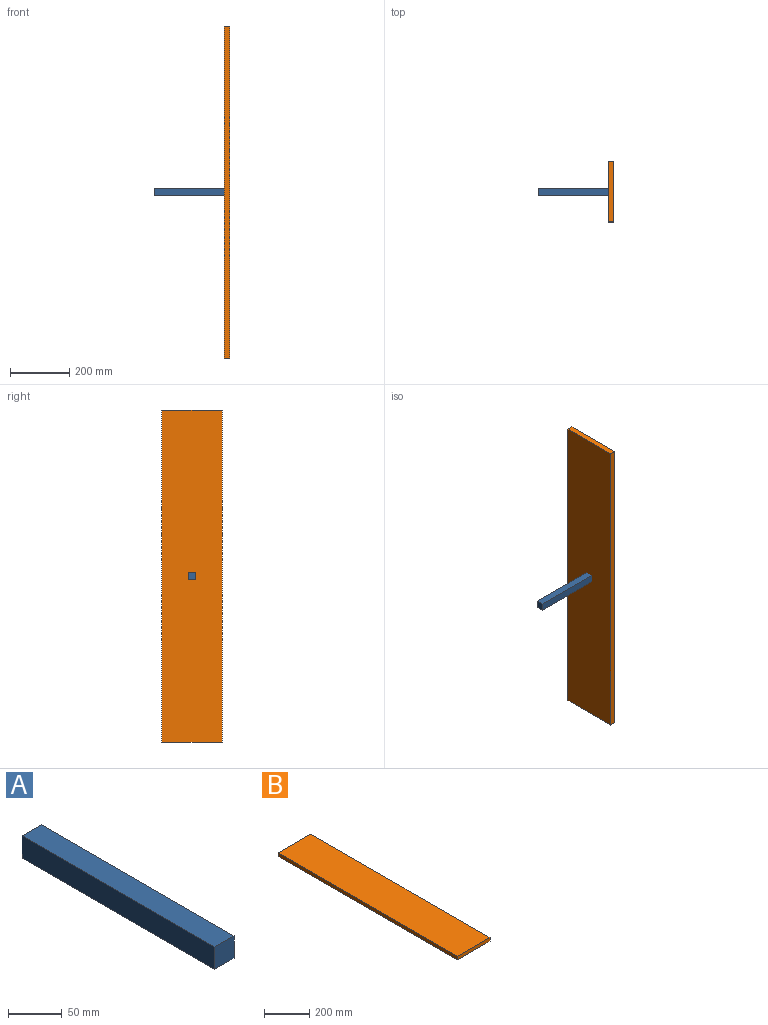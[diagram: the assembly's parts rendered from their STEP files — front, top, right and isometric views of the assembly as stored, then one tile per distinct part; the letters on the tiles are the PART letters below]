
ASSEMBLY  parts=2 mates=1
PART A: 6 faces, bbox 25.4x254x25.4 mm
  f0: plane 25.4x25.4mm, normal (0,-1,0), area 645.2mm2, adj f1,f3,f4,f5
  f1: plane 254x25.4mm, normal (0,0,-1), area 6451.6mm2, adj f0,f2,f4,f5
  f2: plane 25.4x25.4mm, normal (0,1,0), area 645.2mm2, adj f1,f3,f4,f5
  f3: plane 254x25.4mm, normal (0,0,1), area 6451.6mm2, adj f0,f2,f4,f5
  f4: plane 254x25.4mm, normal (1,0,0), area 6451.6mm2, adj f0,f1,f2,f3
  f5: plane 254x25.4mm, normal (-1,0,0), area 6451.6mm2, adj f0,f1,f2,f3
PART B: 6 faces, bbox 203.2x1117.6x19.1 mm
  f0: plane 1117.6x19.05mm, normal (-1,0,0), area 21290.3mm2, adj f1,f3,f4,f5
  f1: plane 1117.6x203.2mm, normal (0,0,-1), area 227096.3mm2, adj f0,f2,f4,f5
  f2: plane 1117.6x19.05mm, normal (1,0,0), area 21290.3mm2, adj f1,f3,f4,f5
  f3: plane 1117.6x203.2mm, normal (0,0,1), area 227096.3mm2, adj f0,f2,f4,f5
  f4: plane 203.2x19.05mm, normal (0,-1,0), area 3871mm2, adj f0,f1,f2,f3
  f5: plane 203.2x19.05mm, normal (0,1,0), area 3871mm2, adj f0,f1,f2,f3
PLACE A rot(axis=(0.58,-0.58,0.58),120deg) t=(-125.4,20.2,-2.84)mm
PLACE B rot(axis=(0.58,0.58,0.58),120deg) t=(-17.45,-11.55,9.86)mm
MATE planar B.f3 <-> A.f0  axis (1,0,0) through (1.6,-11.55,9.86)mm
